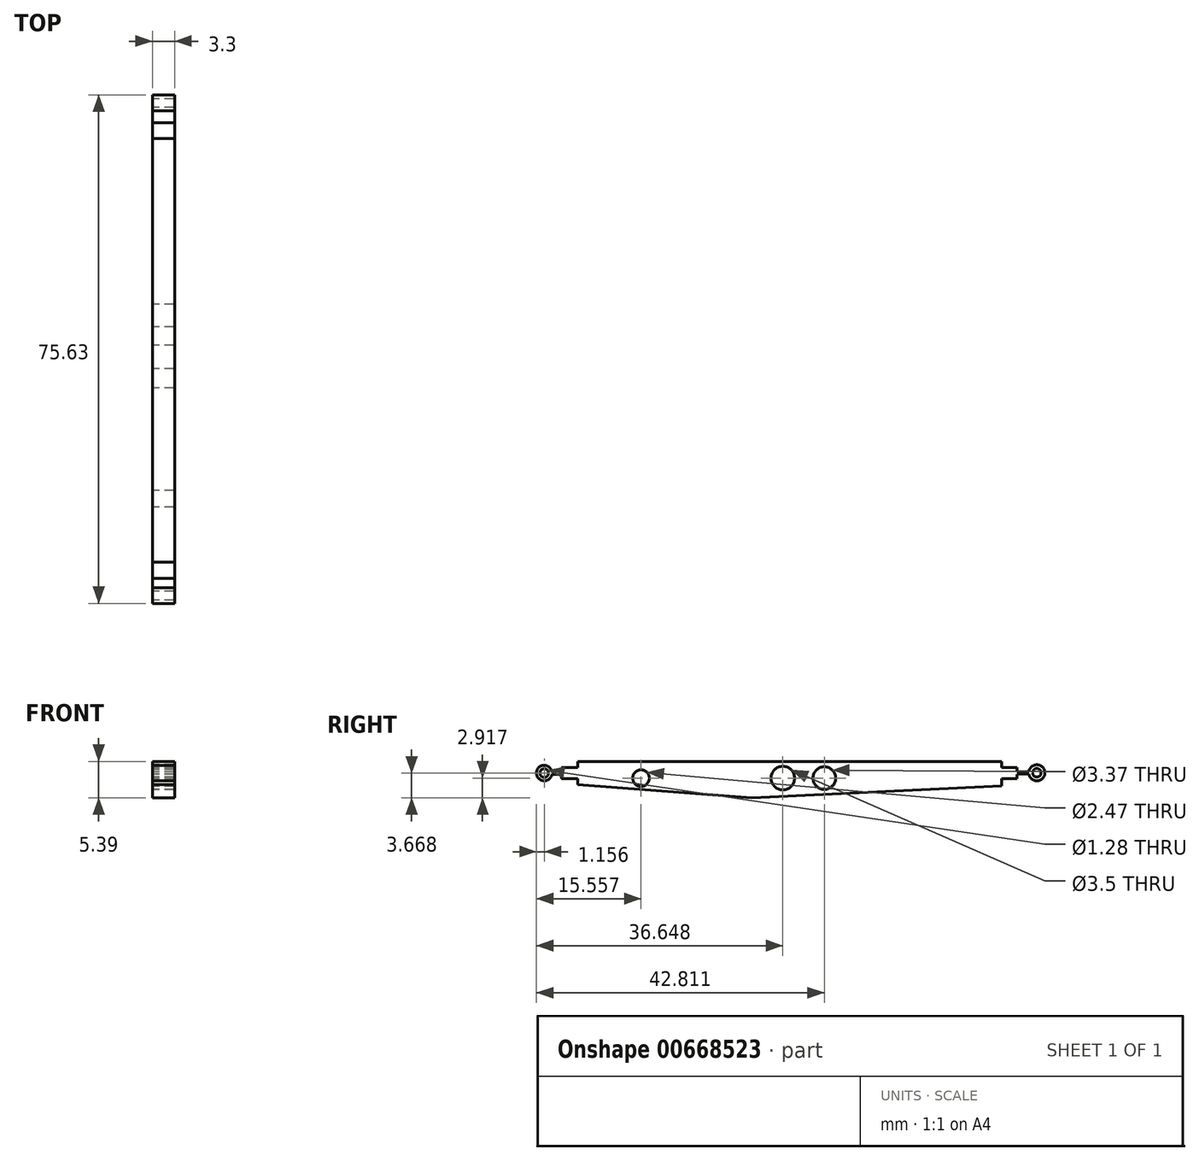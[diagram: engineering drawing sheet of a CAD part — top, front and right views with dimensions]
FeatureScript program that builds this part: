
annotation { "Feature Type Name" : "Feature", "Feature Type Description" : "" }
export const myFeature = defineFeature(function(context is Context, id is Id, definition is map)
    precondition{}
    {
        {
            var Q0;
            Q0=qCreatedBy(makeId("Right.planeOp"),FACE);
            var sketch = newSketch(context, id + "F0", { "sketchPlane" : qUnion([Q0])});
            skLineSegment(sketch, "E0", {"start": v(0, 0) * mm, "end": v(-32.94, 0) * mm});
            skLineSegment(sketch, "E1", {"start": v(0, 0) * mm, "end": v(30.11, 0) * mm});
            skLineSegment(sketch, "E2", {"start": v(30.11, 0) * mm, "end": v(30.11, -3.62) * mm});
            skLineSegment(sketch, "E3", {"start": v(30.11, -3.62) * mm, "end": v(-6.98, -5.39) * mm});
            skLineSegment(sketch, "E4", {"start": v(-32.94, 0) * mm, "end": v(-32.94, -3.44) * mm});
            skLineSegment(sketch, "E5", {"start": v(-32.94, -3.44) * mm, "end": v(-6.98, -5.39) * mm});
            skLineSegment(sketch, "E6.bottom", {"start": v(30.11, -0.88) * mm, "end": v(32.41, -0.88) * mm});
            skLineSegment(sketch, "E6.top", {"start": v(30.11, -2.56) * mm, "end": v(32.41, -2.56) * mm});
            skLineSegment(sketch, "E6.left", {"start": v(30.11, -0.88) * mm, "end": v(30.11, -2.56) * mm});
            skLineSegment(sketch, "E6.right", {"start": v(32.41, -0.88) * mm, "end": v(32.41, -2.56) * mm});
            skLineSegment(sketch, "E7.bottom", {"start": v(-32.94, -0.88) * mm, "end": v(-35.32, -0.88) * mm});
            skLineSegment(sketch, "E7.top", {"start": v(-32.94, -2.56) * mm, "end": v(-35.32, -2.56) * mm});
            skLineSegment(sketch, "E7.left", {"start": v(-32.94, -0.88) * mm, "end": v(-32.94, -2.56) * mm});
            skLineSegment(sketch, "E7.right", {"start": v(-35.32, -0.88) * mm, "end": v(-35.32, -2.56) * mm});
            skLineSegment(sketch, "E8", {"start": v(-35.32, -1.72) * mm, "end": v(-36.74, -1.72) * mm});
            skLineSegment(sketch, "E9", {"start": v(32.41, -1.72) * mm, "end": v(34.18, -1.72) * mm});
            skCircle(sketch, "E10", {"center": v(35.38, -1.68) * mm, "radius": 1.2 * mm});
            skCircle(sketch, "E11", {"center": v(35.38, -1.68) * mm, "radius": 0.63 * mm});
            skCircle(sketch, "E12", {"center": v(-37.9, -1.72) * mm, "radius": 1.16 * mm});
            skCircle(sketch, "E13", {"center": v(-37.9, -1.72) * mm, "radius": 0.64 * mm});
            skLineSegment(sketch, "E14", {"start": v(-36.75, -1.56) * mm, "end": v(-35.32, -1.56) * mm});
            skLineSegment(sketch, "E15", {"start": v(-35.32, -1.56) * mm, "end": v(-35.32, -1.9) * mm});
            skLineSegment(sketch, "E16", {"start": v(-35.32, -1.9) * mm, "end": v(-36.75, -1.9) * mm});
            skLineSegment(sketch, "E17", {"start": v(32.41, -1.9) * mm, "end": v(34.2, -1.87) * mm});
            skLineSegment(sketch, "E18", {"start": v(34.2, -1.87) * mm, "end": v(34.2, -1.56) * mm});
            skLineSegment(sketch, "E19", {"start": v(34.2, -1.56) * mm, "end": v(32.41, -1.56) * mm});
            skCircle(sketch, "E20", {"center": v(-2.4, -2.47) * mm, "radius": 1.75 * mm});
            skCircle(sketch, "E21", {"center": v(-2.4, -2.47) * mm, "radius": 1.39 * mm});
            skCircle(sketch, "E22", {"center": v(3.76, -2.47) * mm, "radius": 1.68 * mm});
            skCircle(sketch, "E23", {"center": v(3.76, -2.47) * mm, "radius": 1.23 * mm});
            skCircle(sketch, "E24", {"center": v(-23.5, -2.47) * mm, "radius": 1.23 * mm});
            skCircle(sketch, "E25", {"center": v(-23.5, -2.47) * mm, "radius": 0.9 * mm});
            skSolve(sketch);
        }
        {
            var Q0;
            Q0 = qSketchRegion(id + "F0", true);
            extrude(context, id + "F1", {"entities" : qUnion([Q0]), "depth" : 3.3 * mm, "offsetDistance" : 25.4 * mm});
        }
    });
